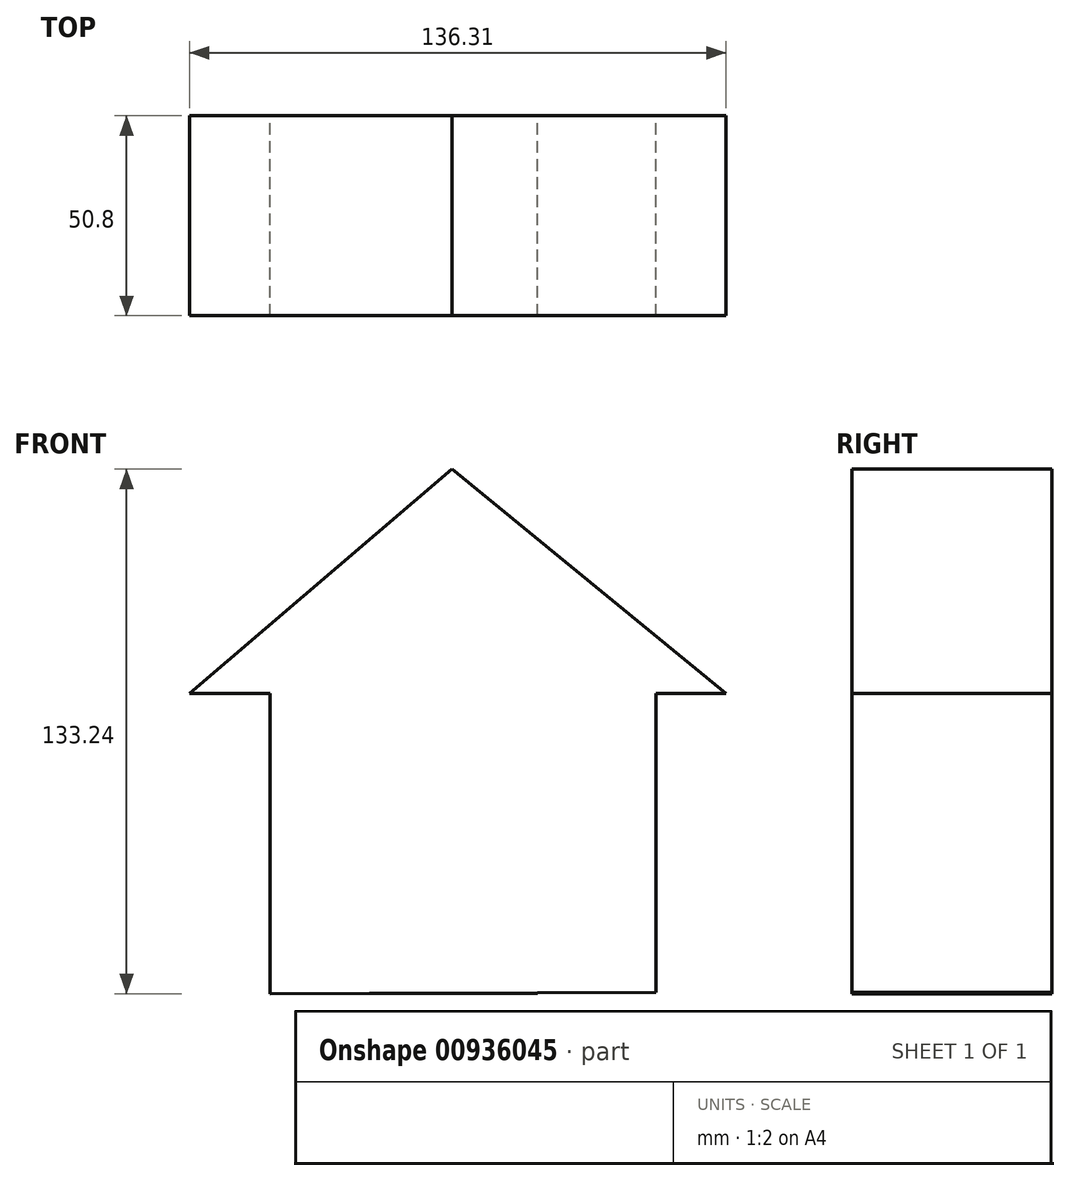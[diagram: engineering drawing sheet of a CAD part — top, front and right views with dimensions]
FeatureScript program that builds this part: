
annotation { "Feature Type Name" : "Feature", "Feature Type Description" : "" }
export const myFeature = defineFeature(function(context is Context, id is Id, definition is map)
    precondition{}
    {
        {
            var Q0;
            Q0=qCreatedBy(makeId("Front.planeOp"),FACE);
            var sketch = newSketch(context, id + "F0", { "sketchPlane" : qUnion([Q0])});
            skLineSegment(sketch, "E0", {"start": v(-46.17, 0) * mm, "end": v(51.89, 0) * mm});
            skLineSegment(sketch, "E1", {"start": v(-46.17, 0) * mm, "end": v(-46.17, -76.25) * mm});
            skLineSegment(sketch, "E2", {"start": v(51.89, 0) * mm, "end": v(51.89, -75.95) * mm});
            skLineSegment(sketch, "E3", {"start": v(-46.17, -76.25) * mm, "end": v(51.89, -75.95) * mm});
            skLineSegment(sketch, "E4.bottom", {"start": v(-20.91, -76.17) * mm, "end": v(21.81, -76.17) * mm});
            skLineSegment(sketch, "E4.top", {"start": v(-20.91, -21.54) * mm, "end": v(21.81, -21.54) * mm});
            skLineSegment(sketch, "E4.left", {"start": v(-20.91, -76.17) * mm, "end": v(-20.91, -21.54) * mm});
            skLineSegment(sketch, "E4.right", {"start": v(21.81, -76.17) * mm, "end": v(21.81, -21.54) * mm});
            skLineSegment(sketch, "E5", {"start": v(-66.65, 0) * mm, "end": v(0, 57) * mm});
            skLineSegment(sketch, "E6", {"start": v(0, 57) * mm, "end": v(69.66, 0) * mm});
            skLineSegment(sketch, "E7", {"start": v(-66.65, 0) * mm, "end": v(-46.17, 0) * mm});
            skLineSegment(sketch, "E8", {"start": v(69.66, 0) * mm, "end": v(51.89, 0) * mm});
            skSolve(sketch);
        }
        {
            var Q0;
            Q0 = qSketchRegion(id + "F0", true);
            extrude(context, id + "F1", {"entities" : qUnion([Q0]), "depth" : 50.8 * mm, "offsetDistance" : 25.4 * mm});
        }
    });
